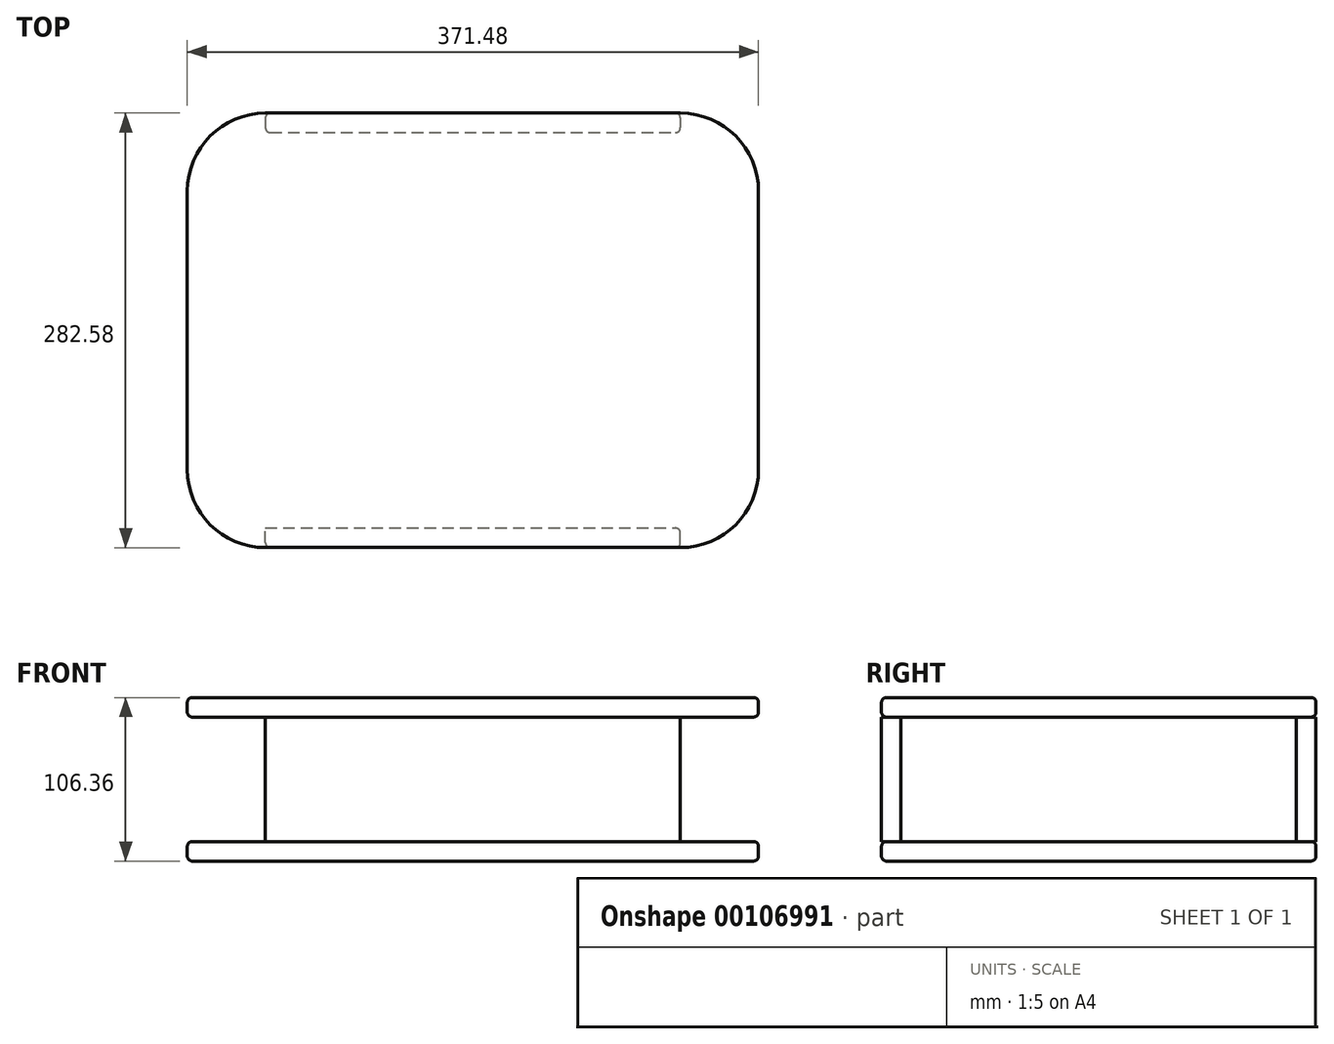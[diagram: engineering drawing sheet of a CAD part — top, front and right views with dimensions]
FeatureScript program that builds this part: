
annotation { "Feature Type Name" : "Feature", "Feature Type Description" : "" }
export const myFeature = defineFeature(function(context is Context, id is Id, definition is map)
    precondition{}
    {
        {
            var Q0;
            Q0=qCreatedBy(makeId("Top.planeOp"),FACE);
            var sketch = newSketch(context, id + "F0", { "sketchPlane" : qUnion([Q0])});
            skLineSegment(sketch, "E0.bottom", {"start": v(134.94, -141.29) * mm, "end": v(-134.94, -141.29) * mm});
            skLineSegment(sketch, "E0.top", {"start": v(134.94, 141.29) * mm, "end": v(-134.94, 141.29) * mm});
            skLineSegment(sketch, "E0.left", {"start": v(185.74, -90.49) * mm, "end": v(185.74, 90.49) * mm});
            skLineSegment(sketch, "E0.right", {"start": v(-185.74, -90.49) * mm, "end": v(-185.74, 90.49) * mm});
            skPoint(sketch, "E0.middle", {"position": v(0, 0) * mm});
            skPoint(sketch, "E1.visualSharp", {"position": v(-185.74, 141.29) * mm});
            skArc(sketch, "E1.filletArc", {"start": v(-134.94, 141.29) * mm, "mid": v(-170.86, 126.4) * mm, "end": v(-185.74, 90.49) * mm});
            skPoint(sketch, "E2.visualSharp", {"position": v(185.74, 141.29) * mm});
            skArc(sketch, "E2.filletArc", {"start": v(185.74, 90.49) * mm, "mid": v(170.86, 126.4) * mm, "end": v(134.94, 141.29) * mm});
            skPoint(sketch, "E3.visualSharp", {"position": v(185.74, -141.29) * mm});
            skArc(sketch, "E3.filletArc", {"start": v(134.94, -141.29) * mm, "mid": v(170.86, -126.4) * mm, "end": v(185.74, -90.49) * mm});
            skPoint(sketch, "E4.visualSharp", {"position": v(-185.74, -141.29) * mm});
            skArc(sketch, "E4.filletArc", {"start": v(-185.74, -90.49) * mm, "mid": v(-170.86, -126.4) * mm, "end": v(-134.94, -141.29) * mm});
            skSolve(sketch);
        }
        {
            var Q0;
            Q0=makeQuery(id+"F0.imprint","IMPRINT",FACE,{"disambiguationData":[TD([[makeQuery(id+"F0.imprint","IMPRINT",EDGE,{"derivedFrom":sQuery(id+"F0.wireOp",EDGE,"E0.bottom")}),-1.0]])]});
            extrude(context, id + "F1", {"entities" : qUnion([Q0]), "depth" : 12.7 * mm});
        }
        {
            var Q0;
            Q0=makeQuery(id+"F1.opExtrude","CAP_FACE",FACE,{"disambiguationData":[OSD([sQuery(id+"F0.wireOp",EDGE,"E0.bottom"),sQuery(id+"F0.wireOp",EDGE,"E0.top"),sQuery(id+"F0.wireOp",EDGE,"E0.left"),sQuery(id+"F0.wireOp",EDGE,"E0.right"),sQuery(id+"F0.wireOp",EDGE,"E1.filletArc"),sQuery(id+"F0.wireOp",EDGE,"E2.filletArc"),sQuery(id+"F0.wireOp",EDGE,"E3.filletArc"),sQuery(id+"F0.wireOp",EDGE,"E4.filletArc")])],"isStart":false});
            var sketch = newSketch(context, id + "F2", { "sketchPlane" : qUnion([Q0])});
            skLineSegment(sketch, "E5.bottom", {"start": v(-134.94, -141.29) * mm, "end": v(134.94, -141.29) * mm});
            skLineSegment(sketch, "E5.top", {"start": v(-134.94, -128.59) * mm, "end": v(134.94, -128.59) * mm});
            skLineSegment(sketch, "E5.left", {"start": v(-134.94, -141.29) * mm, "end": v(-134.94, -128.59) * mm});
            skLineSegment(sketch, "E5.right", {"start": v(134.94, -141.29) * mm, "end": v(134.94, -128.59) * mm});
            skLineSegment(sketch, "E6.bottom", {"start": v(-134.94, 141.29) * mm, "end": v(134.94, 141.29) * mm});
            skLineSegment(sketch, "E6.top", {"start": v(-134.94, 128.59) * mm, "end": v(134.94, 128.59) * mm});
            skLineSegment(sketch, "E6.left", {"start": v(-134.94, 141.29) * mm, "end": v(-134.94, 128.59) * mm});
            skLineSegment(sketch, "E6.right", {"start": v(134.94, 141.29) * mm, "end": v(134.94, 128.59) * mm});
            skSolve(sketch);
        }
        {
            var Q0;
            Q0=makeQuery(id+"F2.imprint","IMPRINT",FACE,{"disambiguationData":[TD([[makeQuery(id+"F2.imprint","IMPRINT",EDGE,{"derivedFrom":sQuery(id+"F2.wireOp",EDGE,"E6.bottom")}),1.0]])]});
            var Q1;
            Q1=makeQuery(id+"F2.imprint","IMPRINT",FACE,{"disambiguationData":[TD([[makeQuery(id+"F2.imprint","IMPRINT",EDGE,{"derivedFrom":sQuery(id+"F2.wireOp",EDGE,"E5.bottom")}),-1.0]])]});
            extrude(context, id + "F3", {"entities" : qUnion([Q0, Q1]), "depth" : 80.96 * mm});
        }
        {
            var Q0;
            Q0=makeQuery(id+"F1.opExtrude","SWEPT_BODY",BODY,{"disambiguationData":[OSD([sQuery(id+"F0.wireOp",EDGE,"E0.bottom"),sQuery(id+"F0.wireOp",EDGE,"E0.top"),sQuery(id+"F0.wireOp",EDGE,"E0.left"),sQuery(id+"F0.wireOp",EDGE,"E0.right"),sQuery(id+"F0.wireOp",EDGE,"E1.filletArc"),sQuery(id+"F0.wireOp",EDGE,"E2.filletArc"),sQuery(id+"F0.wireOp",EDGE,"E3.filletArc"),sQuery(id+"F0.wireOp",EDGE,"E4.filletArc")])]});
            var Q1;
            Q1=makeQuery(id+"F1.opExtrude","SWEPT_EDGE",EDGE,{"disambiguationData":[OSD([sQuery(id+"F0.wireOp",EDGE,"E0.bottom"),sQuery(id+"F0.wireOp",EDGE,"E4.filletArc")])]});
            var Q2;
            Q2=makeQuery(id+"F3.opExtrude","SWEPT_EDGE",EDGE,{"disambiguationData":[OSD([sQuery(id+"F0.wireOp",EDGE,"E4.filletArc"),sQuery(id+"F2.wireOp",EDGE,"E5.bottom"),sQuery(id+"F2.wireOp",EDGE,"E5.left")])]});
            var Q3;
            Q3=makeQuery(id+"F3.opExtrude","SWEPT_EDGE",EDGE,{"disambiguationData":[OSD([sQuery(id+"F0.wireOp",EDGE,"E4.filletArc"),sQuery(id+"F2.wireOp",EDGE,"E5.bottom"),sQuery(id+"F2.wireOp",EDGE,"E5.left")])]});
            transform(context, id + "F4", {"entities" : qUnion([Q0]), "transformType" : TransformType.TRANSLATION_DISTANCE, "transformDirection" : qUnion([Q3]), "distance" : 93.66 * mm, "oppositeDirection" : true, "makeCopy" : true});
        }
        {
            var Q0;
            Q0=makeQuery(id+"F4.opPattern","COPY",EDGE,{"derivedFrom":makeQuery(id+"F1.opExtrude","CAP_EDGE",EDGE,{"disambiguationData":[OSD([sQuery(id+"F0.wireOp",EDGE,"E0.bottom")])],"isStart":false}),"instanceName":"1"});
            var Q1;
            Q1=makeQuery(id+"F4.opPattern","COPY",EDGE,{"derivedFrom":makeQuery(id+"F1.opExtrude","CAP_EDGE",EDGE,{"disambiguationData":[OSD([sQuery(id+"F0.wireOp",EDGE,"E4.filletArc")])],"isStart":true}),"instanceName":"1"});
            var Q2;
            Q2=makeQuery(id+"F1.opExtrude","CAP_EDGE",EDGE,{"disambiguationData":[OSD([sQuery(id+"F0.wireOp",EDGE,"E0.bottom")])],"isStart":true});
            var Q3;
            Q3=makeQuery(id+"F1.opExtrude","CAP_EDGE",EDGE,{"disambiguationData":[OSD([sQuery(id+"F0.wireOp",EDGE,"E4.filletArc")])],"isStart":false});
            var Q4;
            Q4=makeQuery(id+"F3.opExtrude","SWEPT_EDGE",EDGE,{"disambiguationData":[OSD([sQuery(id+"F0.wireOp",EDGE,"E4.filletArc"),sQuery(id+"F2.wireOp",EDGE,"E5.bottom"),sQuery(id+"F2.wireOp",EDGE,"E5.left")])]});
            var Q5;
            Q5=makeQuery(id+"F3.opExtrude","SWEPT_EDGE",EDGE,{"disambiguationData":[OSD([sQuery(id+"F0.wireOp",EDGE,"E3.filletArc"),sQuery(id+"F2.wireOp",EDGE,"E5.bottom"),sQuery(id+"F2.wireOp",EDGE,"E5.right")])]});
            var Q6;
            Q6=makeQuery(id+"F3.opExtrude","SWEPT_EDGE",EDGE,{"disambiguationData":[OSD([sQuery(id+"F2.wireOp",EDGE,"E5.top"),sQuery(id+"F2.wireOp",EDGE,"E5.right")])]});
            var Q7;
            Q7=makeQuery(id+"F3.opExtrude","SWEPT_EDGE",EDGE,{"disambiguationData":[OSD([sQuery(id+"F0.wireOp",EDGE,"E2.filletArc"),sQuery(id+"F2.wireOp",EDGE,"E6.bottom"),sQuery(id+"F2.wireOp",EDGE,"E6.right")])]});
            var Q8;
            Q8=makeQuery(id+"F3.opExtrude","SWEPT_EDGE",EDGE,{"disambiguationData":[OSD([sQuery(id+"F2.wireOp",EDGE,"E6.top"),sQuery(id+"F2.wireOp",EDGE,"E6.right")])]});
            var Q9;
            Q9=makeQuery(id+"F3.opExtrude","SWEPT_EDGE",EDGE,{"disambiguationData":[OSD([sQuery(id+"F0.wireOp",EDGE,"E1.filletArc"),sQuery(id+"F2.wireOp",EDGE,"E6.bottom"),sQuery(id+"F2.wireOp",EDGE,"E6.left")])]});
            var Q10;
            Q10=makeQuery(id+"F3.opExtrude","SWEPT_EDGE",EDGE,{"disambiguationData":[OSD([sQuery(id+"F2.wireOp",EDGE,"E6.top"),sQuery(id+"F2.wireOp",EDGE,"E6.left")])]});
            fillet(context, id + "F5", {"entities" : qUnion([Q0, Q1, Q2, Q3, Q4, Q5, Q6, Q7, Q8, Q9, Q10]), "radius" : 3.17 * mm, "tangentPropagation" : true, "allowEdgeOverflow" : false});
        }
    });
